# Revit family: 304_753c4a26f6b74715b10d23254806cf
name_source: partatom
category: Pipe Accessories
revit_build: Autodesk Revit 2018 (Build: 20170223_1515(x64)
units: mm (PartAtom-declared; Revit-internal decimal feet)

## family parameters
Always vertical = Yes
Cut with Voids When Loaded = No
Part Type = Valve - Breaks Into
Round Connector Dimension = Use Diameter
Shared = No
Work Plane-Based = No

## types (4) — shared parameters
ANGLE = 28.00°
CAT0 = Yes
Description = DZR brass pressure independent control valve (PICV) PN20
H3 = 8 mm  [stored 0.0262467 ft]
H5 = 26 mm  [stored 0.0853018 ft]
H5__ve = -26 mm  [stored -0.0853018 ft]
L2D = 67 mm
L2D_Min = 3048 mm
Manufacturer = VIR
QmdConnectorList = 301;D;302;D
R15 = 20 mm  [stored 0.0656168 ft]
R7 = 8 mm  [stored 0.0262467 ft]
R8 = 5 mm  [stored 0.0164042 ft]
URL = http://www.vironline.com
W2D = 15 mm  [stored 0.0492126 ft]
magiPartTypeId = 304
magiProductFamilyId = 753c4a26f6b74715b10d23254806cf
zero-valued in all types: L4

## per-type parameters (varying)
- 9705 DN15: D=15 mm; H1=24 mm; H10=6 mm  [stored 0.019685 ft]; H12=9 mm  [stored 0.0295276 ft]; H12__ve=-9 mm; H14=17 mm  [stored 0.0557743 ft]; H14__ve=-17 mm; H15=31 mm; H15__ve=-31 mm; H16=10 mm  [stored 0.0328084 ft]; H16__ve=-10 mm  [stored -0.0328084 ft]; H17=5 mm  [stored 0.0164042 ft]; H18=9 mm  [stored 0.0295276 ft]; H19=17 mm  [stored 0.0557743 ft]; H1__ve=-24 mm; H2=6 mm  [stored 0.019685 ft]; H4=11 mm  [stored 0.0360892 ft]; H4__ve=-11 mm; L1=6 mm  [stored 0.019685 ft]; L2=3 mm  [stored 0.00984252 ft]; L6=13 mm; L7=18 mm; L_2=33 mm; R1=8 mm  [stored 0.0262467 ft]; R12=12 mm  [stored 0.0393701 ft]; R14=14 mm  [stored 0.0459318 ft]; R2=12 mm  [stored 0.0393701 ft]; R6=4 mm  [stored 0.0131234 ft]; W_2=22 mm; magiProductId=4728afde89994077b9ff045beeefe4
- 9705 DN20: D=20 mm; H1=27 mm  [stored 0.0885827 ft]; H10=9 mm  [stored 0.0295276 ft]; H12=11 mm  [stored 0.0360892 ft]; H12__ve=-11 mm; H14=20 mm  [stored 0.0656168 ft]; H14__ve=-20 mm  [stored -0.0656168 ft]; H15=32 mm; H15__ve=-32 mm; H16=10 mm  [stored 0.0328084 ft]; H16__ve=-10 mm  [stored -0.0328084 ft]; H17=5 mm  [stored 0.0164042 ft]; H18=10 mm  [stored 0.0328084 ft]; H19=18 mm; H1__ve=-27 mm  [stored -0.0885827 ft]; H2=9 mm  [stored 0.0295276 ft]; H4=16 mm  [stored 0.0524934 ft]; H4__ve=-16 mm; L1=7 mm  [stored 0.0229659 ft]; L2=3 mm  [stored 0.00984252 ft]; L6=16 mm  [stored 0.0524934 ft]; L7=21 mm; L_2=39 mm; R1=11 mm  [stored 0.0360892 ft]; R12=15 mm  [stored 0.0492126 ft]; R14=17 mm  [stored 0.0557743 ft]; R2=14 mm  [stored 0.0459318 ft]; R6=4 mm  [stored 0.0131234 ft]; W_2=26 mm  [stored 0.0853018 ft]; magiProductId=bfc35f7c5b8b4fa0826a13429cda09
- 9705 DN25: D=25 mm; H1=30 mm; H10=12 mm  [stored 0.0393701 ft]; H12=13 mm; H12__ve=-13 mm; H14=23 mm; H14__ve=-23 mm; H15=44 mm; H15__ve=-44 mm; H16=13 mm; H16__ve=-13 mm; H17=6 mm  [stored 0.019685 ft]; H18=12 mm  [stored 0.0393701 ft]; H19=22 mm; H1__ve=-30 mm; H2=12 mm  [stored 0.0393701 ft]; H4=22 mm; H4__ve=-22 mm; L1=8 mm  [stored 0.0262467 ft]; L2=4 mm  [stored 0.0131234 ft]; L6=20 mm  [stored 0.0656168 ft]; L7=26 mm  [stored 0.0853018 ft]; L_2=49 mm; R1=14 mm  [stored 0.0459318 ft]; R12=18 mm; R14=20 mm  [stored 0.0656168 ft]; R2=17 mm  [stored 0.0557743 ft]; R6=8 mm  [stored 0.0262467 ft]; W_2=30 mm; magiProductId=683b7e39614846839e59e3182d6b60
- 9705 L-DN15: D=15 mm; H1=24 mm; H10=6 mm  [stored 0.019685 ft]; H12=9 mm  [stored 0.0295276 ft]; H12__ve=-9 mm; H14=17 mm  [stored 0.0557743 ft]; H14__ve=-17 mm; H15=31 mm; H15__ve=-31 mm; H16=10 mm  [stored 0.0328084 ft]; H16__ve=-10 mm  [stored -0.0328084 ft]; H17=5 mm  [stored 0.0164042 ft]; H18=9 mm  [stored 0.0295276 ft]; H19=17 mm  [stored 0.0557743 ft]; H1__ve=-24 mm; H2=6 mm  [stored 0.019685 ft]; H4=11 mm  [stored 0.0360892 ft]; H4__ve=-11 mm; L1=6 mm  [stored 0.019685 ft]; L2=3 mm  [stored 0.00984252 ft]; L6=13 mm; L7=18 mm; L_2=33 mm; R1=8 mm  [stored 0.0262467 ft]; R12=12 mm  [stored 0.0393701 ft]; R14=14 mm  [stored 0.0459318 ft]; R2=12 mm  [stored 0.0393701 ft]; R6=4 mm  [stored 0.0131234 ft]; W_2=22 mm; magiProductId=2acdf034af88458a8ddbf54a8840df

note: column(s) folded — value = type name in every type: MC Product Code

note: [stored X ft] marks values corroborated as IEEE doubles in the binary element streams (Revit-internal decimal feet)

## geometry (parser evidence)
native form markers: Sweep x1
no freeform markers — native parametric forms only
